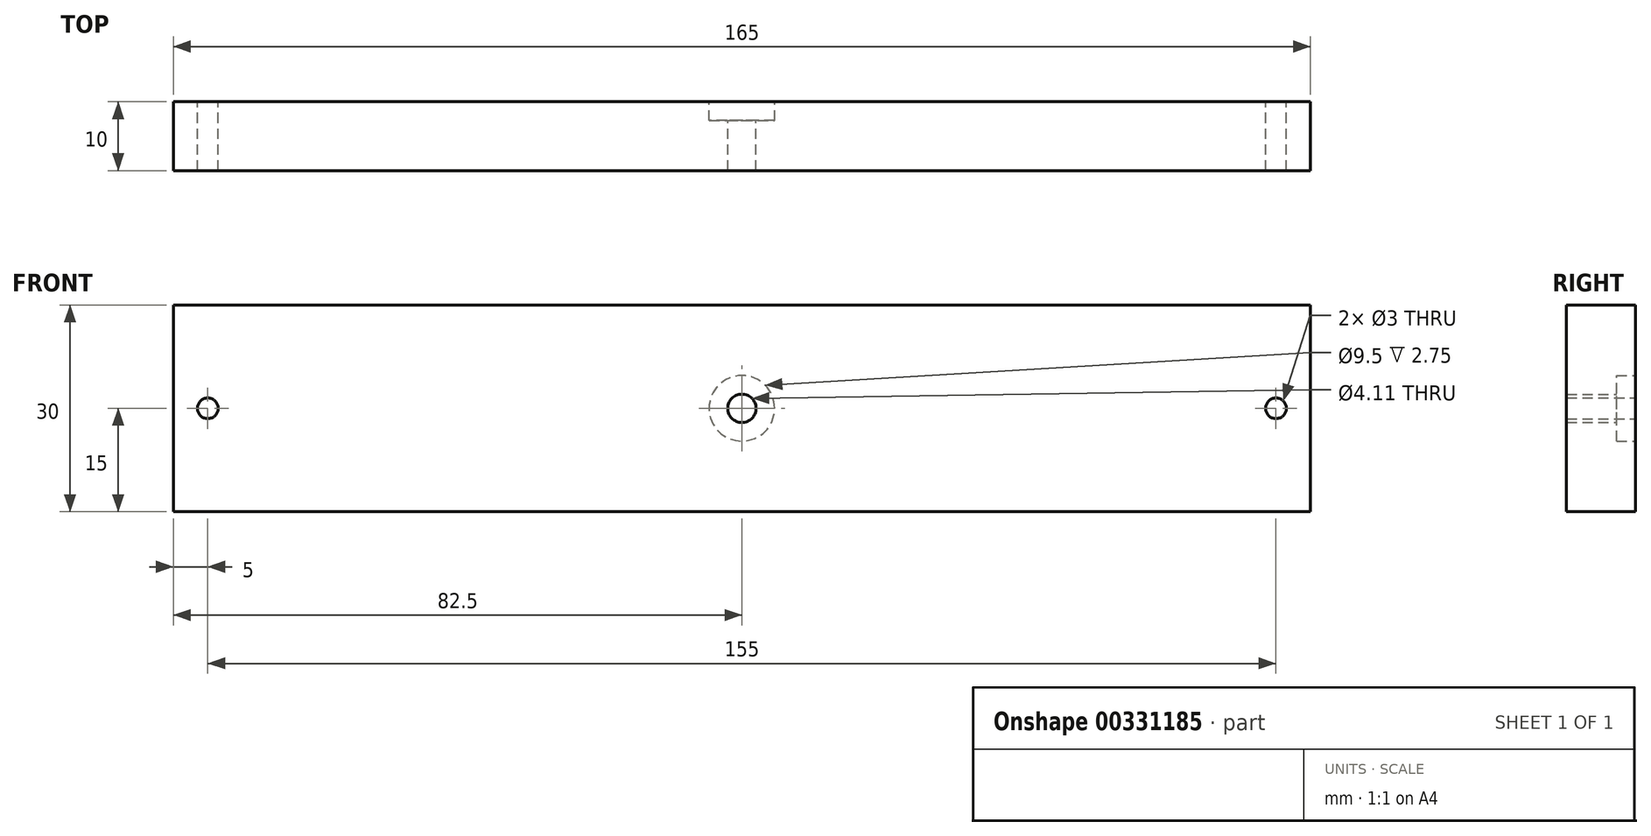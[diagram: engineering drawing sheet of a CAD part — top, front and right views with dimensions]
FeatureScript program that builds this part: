
annotation { "Feature Type Name" : "Feature", "Feature Type Description" : "" }
export const myFeature = defineFeature(function(context is Context, id is Id, definition is map)
    precondition{}
    {
        {
            var Q0;
            Q0=qCreatedBy(makeId("Front.planeOp"),FACE);
            var sketch = newSketch(context, id + "F0", { "sketchPlane" : qUnion([Q0])});
            skLineSegment(sketch, "E0.bottom", {"start": v(82.5, 15) * mm, "end": v(-82.5, 15) * mm});
            skLineSegment(sketch, "E0.top", {"start": v(82.5, -15) * mm, "end": v(-82.5, -15) * mm});
            skLineSegment(sketch, "E0.left", {"start": v(82.5, 15) * mm, "end": v(82.5, -15) * mm});
            skLineSegment(sketch, "E0.right", {"start": v(-82.5, 15) * mm, "end": v(-82.5, -15) * mm});
            skPoint(sketch, "E0.middle", {"position": v(0, 0) * mm});
            skPoint(sketch, "E1", {"position": v(-77.5, 0) * mm});
            skPoint(sketch, "E2", {"position": v(77.5, 0) * mm});
            skCircle(sketch, "E3", {"center": v(77.5, 0) * mm, "radius": 1.5 * mm});
            skCircle(sketch, "E4", {"center": v(-77.5, 0) * mm, "radius": 1.5 * mm});
            skPoint(sketch, "E5.orphan", {"position": v(-82.5, 0) * mm});
            skPoint(sketch, "E6.orphan", {"position": v(-72.5, 0) * mm});
            skPoint(sketch, "E7.orphan", {"position": v(82.5, 0) * mm});
            skPoint(sketch, "E8.orphan", {"position": v(72.5, 0) * mm});
            skPoint(sketch, "E9.orphan", {"position": v(-72.5, 15) * mm});
            skPoint(sketch, "E10.end.orphan", {"position": v(-72.5, -15) * mm});
            skPoint(sketch, "E11.orphan", {"position": v(72.5, 15) * mm});
            skPoint(sketch, "E12.end.orphan", {"position": v(72.5, -15) * mm});
            skCircle(sketch, "E13", {"center": v(0, 0) * mm, "radius": 4.75 * mm});
            skCircle(sketch, "E14", {"center": v(0, 0) * mm, "radius": 2.06 * mm});
            skSolve(sketch);
        }
        {
            var Q0;
            Q0=makeQuery(id+"F0.imprint","IMPRINT",FACE,{"disambiguationData":[TD([[makeQuery(id+"F0.imprint","IMPRINT",EDGE,{"derivedFrom":sQuery(id+"F0.wireOp",EDGE,"E0.bottom")}),1.0]])]});
            var Q1;
            Q1=makeQuery(id+"F0.imprint","IMPRINT",FACE,{"disambiguationData":[TD([[makeQuery(id+"F0.imprint","IMPRINT",EDGE,{"derivedFrom":sQuery(id+"F0.wireOp",EDGE,"E13")}),1.0]])]});
            var Q2;
            Q2=makeQuery(id+"F0.imprint","IMPRINT",FACE,{"disambiguationData":[TD([[makeQuery(id+"F0.imprint","IMPRINT",EDGE,{"derivedFrom":sQuery(id+"F0.wireOp",EDGE,"E14")}),1.0]])]});
            extrude(context, id + "F1", {"entities" : qUnion([Q0, Q1, Q2]), "depth" : 10 * mm});
        }
        {
            var Q0;
            Q0=makeQuery(id+"F0.imprint","IMPRINT",FACE,{"disambiguationData":[TD([[makeQuery(id+"F0.imprint","IMPRINT",EDGE,{"derivedFrom":sQuery(id+"F0.wireOp",EDGE,"E13")}),1.0]])]});
            var Q1;
            Q1=makeQuery(id+"F0.imprint","IMPRINT",FACE,{"disambiguationData":[TD([[makeQuery(id+"F0.imprint","IMPRINT",EDGE,{"derivedFrom":sQuery(id+"F0.wireOp",EDGE,"E14")}),1.0]])]});
            extrude(context, id + "F2", {"entities" : qUnion([Q0, Q1]), "operationType" : NewBodyOperationType.REMOVE, "depth" : 2.75 * mm});
        }
        {
            var Q0;
            Q0=makeQuery(id+"F0.imprint","IMPRINT",FACE,{"disambiguationData":[TD([[makeQuery(id+"F0.imprint","IMPRINT",EDGE,{"derivedFrom":sQuery(id+"F0.wireOp",EDGE,"E14")}),1.0]])]});
            extrude(context, id + "F3", {"entities" : qUnion([Q0]), "operationType" : NewBodyOperationType.REMOVE, "depth" : 25 * mm});
        }
    });
